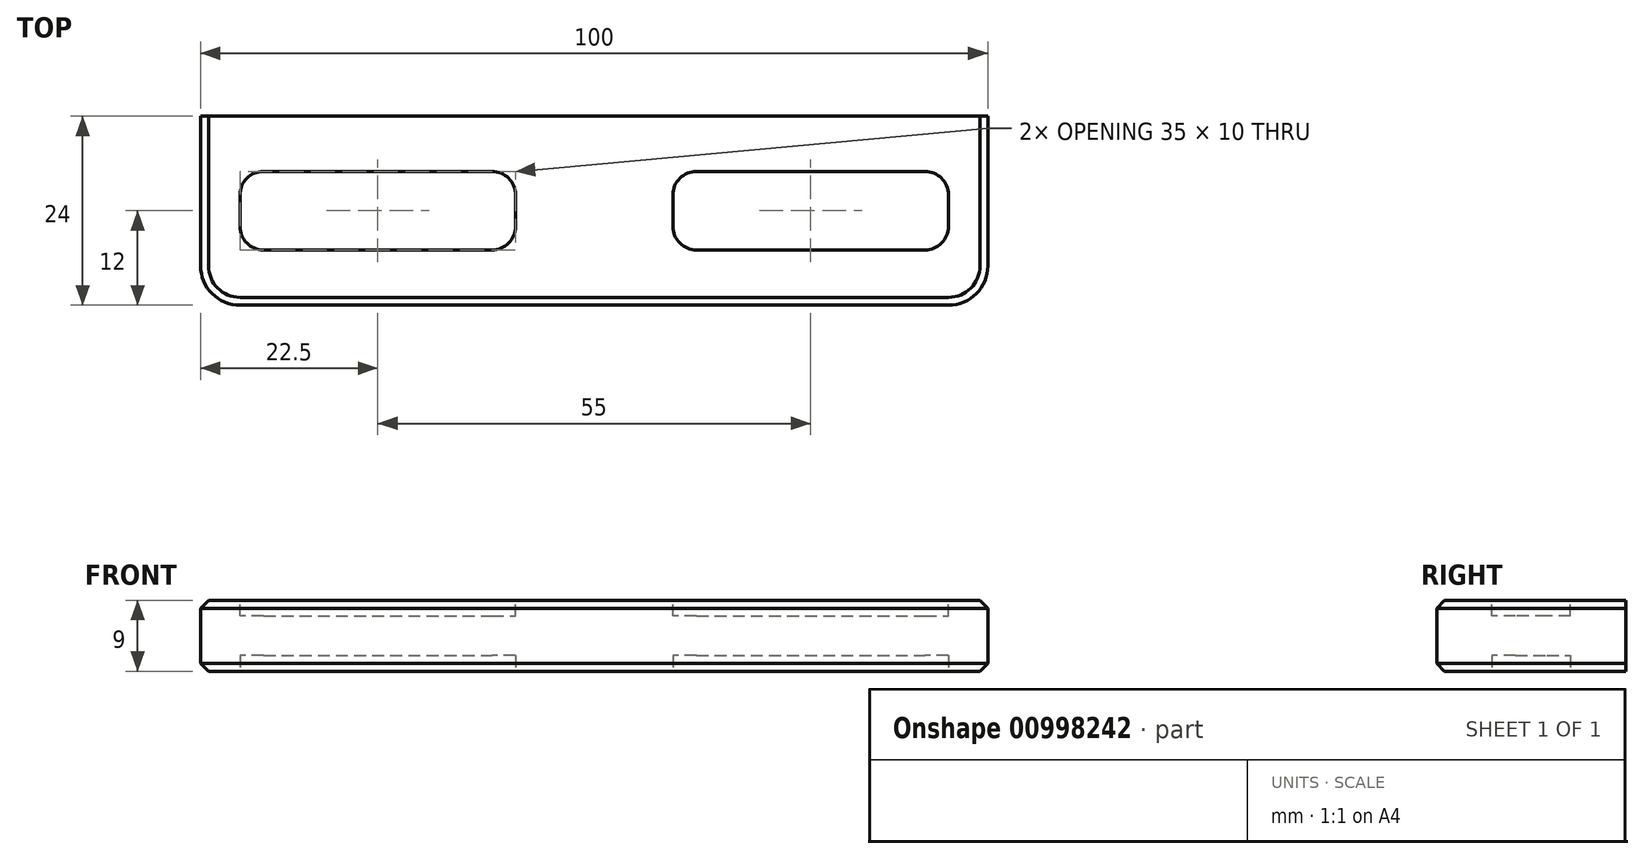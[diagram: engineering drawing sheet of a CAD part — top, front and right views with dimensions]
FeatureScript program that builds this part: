
annotation { "Feature Type Name" : "Feature", "Feature Type Description" : "" }
export const myFeature = defineFeature(function(context is Context, id is Id, definition is map)
    precondition{}
    {
        {
            var Q0;
            Q0=qCreatedBy(makeId("Top.planeOp"),FACE);
            var sketch = newSketch(context, id + "F0", { "sketchPlane" : qUnion([Q0])});
            skLineSegment(sketch, "E0.bottom", {"start": v(-50, 24) * mm, "end": v(50, 24) * mm});
            skLineSegment(sketch, "E0.top", {"start": v(-50, 0) * mm, "end": v(50, 0) * mm});
            skLineSegment(sketch, "E0.left", {"start": v(-50, 24) * mm, "end": v(-50, 0) * mm});
            skLineSegment(sketch, "E0.right", {"start": v(50, 24) * mm, "end": v(50, 0) * mm});
            skSolve(sketch);
        }
        {
            var Q0;
            Q0=makeQuery(id+"F0.imprint","IMPRINT",FACE,{"disambiguationData":[TD([[makeQuery(id+"F0.imprint","IMPRINT",EDGE,{"derivedFrom":sQuery(id+"F0.wireOp",EDGE,"E0.bottom")}),-1.0]])]});
            extrude(context, id + "F1", {"entities" : qUnion([Q0]), "depth" : 9 * mm, "offsetDistance" : 25 * mm});
        }
        {
            var Q0;
            Q0=makeQuery(id+"F1.opExtrude","SWEPT_EDGE",EDGE,{"disambiguationData":[OSD([sQuery(id+"F0.wireOp",EDGE,"E0.top"),sQuery(id+"F0.wireOp",EDGE,"E0.left")])]});
            var Q1;
            Q1=makeQuery(id+"F1.opExtrude","SWEPT_EDGE",EDGE,{"disambiguationData":[OSD([sQuery(id+"F0.wireOp",EDGE,"E0.top"),sQuery(id+"F0.wireOp",EDGE,"E0.right")])]});
            fillet(context, id + "F2", {"entities" : qUnion([Q0, Q1]), "radius" : 5 * mm, "tangentPropagation" : true, "allowEdgeOverflow" : false});
        }
        {
            var Q0;
            Q0=makeQuery(id+"F1.opExtrude","CAP_FACE",FACE,{"disambiguationData":[OSD([sQuery(id+"F0.wireOp",EDGE,"E0.bottom"),sQuery(id+"F0.wireOp",EDGE,"E0.top"),sQuery(id+"F0.wireOp",EDGE,"E0.left"),sQuery(id+"F0.wireOp",EDGE,"E0.right")])],"isStart":false});
            var sketch = newSketch(context, id + "F3", { "sketchPlane" : qUnion([Q0])});
            skLineSegment(sketch, "E1.bottom", {"start": v(-45, 17) * mm, "end": v(-10, 17) * mm});
            skLineSegment(sketch, "E1.top", {"start": v(-45, 7) * mm, "end": v(-10, 7) * mm});
            skLineSegment(sketch, "E1.left", {"start": v(-45, 17) * mm, "end": v(-45, 7) * mm});
            skLineSegment(sketch, "E1.right", {"start": v(-10, 17) * mm, "end": v(-10, 7) * mm});
            skSolve(sketch);
        }
        {
            var Q0;
            Q0=makeQuery(id+"F3.imprint","IMPRINT",FACE,{"disambiguationData":[TD([[makeQuery(id+"F3.imprint","IMPRINT",EDGE,{"derivedFrom":sQuery(id+"F3.wireOp",EDGE,"E1.bottom")}),1.0]])]});
            var sketch = newSketch(context, id + "F4", { "sketchPlane" : qUnion([Q0])});
            skLineSegment(sketch, "E2.bottom", {"start": v(10, 17) * mm, "end": v(45, 17) * mm});
            skLineSegment(sketch, "E2.top", {"start": v(10, 7) * mm, "end": v(45, 7) * mm});
            skLineSegment(sketch, "E2.left", {"start": v(10, 17) * mm, "end": v(10, 7) * mm});
            skLineSegment(sketch, "E2.right", {"start": v(45, 17) * mm, "end": v(45, 7) * mm});
            skSolve(sketch);
        }
        {
            var Q0;
            Q0=makeQuery(id+"F3.imprint","IMPRINT",FACE,{"disambiguationData":[TD([[makeQuery(id+"F3.imprint","IMPRINT",EDGE,{"derivedFrom":sQuery(id+"F3.wireOp",EDGE,"E1.bottom")}),-1.0]])]});
            var Q1;
            Q1=makeQuery(id+"F4.imprint","IMPRINT",FACE,{"disambiguationData":[TD([[makeQuery(id+"F4.imprint","IMPRINT",EDGE,{"derivedFrom":sQuery(id+"F4.wireOp",EDGE,"E2.bottom")}),-1.0]])]});
            extrude(context, id + "F5", {"entities" : qUnion([Q0, Q1]), "operationType" : NewBodyOperationType.REMOVE, "oppositeDirection" : true, "depth" : 2 * mm, "offsetDistance" : 25 * mm});
        }
        {
            var Q0;
            Q0=makeQuery(id+"F5.boolean.opBoolean","COPY",EDGE,{"derivedFrom":makeQuery(id+"F5.opExtrude","SWEPT_EDGE",EDGE,{"disambiguationData":[OSD([sQuery(id+"F3.wireOp",EDGE,"E1.top"),sQuery(id+"F3.wireOp",EDGE,"E1.left")])]})});
            var Q1;
            Q1=makeQuery(id+"F5.boolean.opBoolean","COPY",EDGE,{"derivedFrom":makeQuery(id+"F5.opExtrude","SWEPT_EDGE",EDGE,{"disambiguationData":[OSD([sQuery(id+"F3.wireOp",EDGE,"E1.bottom"),sQuery(id+"F3.wireOp",EDGE,"E1.left")])]})});
            var Q2;
            Q2=makeQuery(id+"F5.boolean.opBoolean","COPY",EDGE,{"derivedFrom":makeQuery(id+"F5.opExtrude","SWEPT_EDGE",EDGE,{"disambiguationData":[OSD([sQuery(id+"F3.wireOp",EDGE,"E1.bottom"),sQuery(id+"F3.wireOp",EDGE,"E1.right")])]})});
            var Q3;
            Q3=makeQuery(id+"F5.boolean.opBoolean","COPY",EDGE,{"derivedFrom":makeQuery(id+"F5.opExtrude","SWEPT_EDGE",EDGE,{"disambiguationData":[OSD([sQuery(id+"F4.wireOp",EDGE,"E2.top"),sQuery(id+"F4.wireOp",EDGE,"E2.left")])]})});
            var Q4;
            Q4=makeQuery(id+"F5.boolean.opBoolean","COPY",EDGE,{"derivedFrom":makeQuery(id+"F5.opExtrude","SWEPT_EDGE",EDGE,{"disambiguationData":[OSD([sQuery(id+"F3.wireOp",EDGE,"E1.top"),sQuery(id+"F3.wireOp",EDGE,"E1.right")])]})});
            var Q5;
            Q5=makeQuery(id+"F5.boolean.opBoolean","COPY",EDGE,{"derivedFrom":makeQuery(id+"F5.opExtrude","SWEPT_EDGE",EDGE,{"disambiguationData":[OSD([sQuery(id+"F4.wireOp",EDGE,"E2.top"),sQuery(id+"F4.wireOp",EDGE,"E2.right")])]})});
            var Q6;
            Q6=makeQuery(id+"F5.boolean.opBoolean","COPY",EDGE,{"derivedFrom":makeQuery(id+"F5.opExtrude","SWEPT_EDGE",EDGE,{"disambiguationData":[OSD([sQuery(id+"F4.wireOp",EDGE,"E2.bottom"),sQuery(id+"F4.wireOp",EDGE,"E2.right")])]})});
            var Q7;
            Q7=makeQuery(id+"F5.boolean.opBoolean","COPY",EDGE,{"derivedFrom":makeQuery(id+"F5.opExtrude","SWEPT_EDGE",EDGE,{"disambiguationData":[OSD([sQuery(id+"F4.wireOp",EDGE,"E2.bottom"),sQuery(id+"F4.wireOp",EDGE,"E2.left")])]})});
            fillet(context, id + "F6", {"entities" : qUnion([Q0, Q1, Q2, Q3, Q4, Q5, Q6, Q7]), "radius" : 3 * mm, "tangentPropagation" : true, "allowEdgeOverflow" : false});
        }
        {
            var Q0;
            Q0=makeQuery(id+"F1.opExtrude","CAP_FACE",FACE,{"disambiguationData":[OSD([sQuery(id+"F0.wireOp",EDGE,"E0.bottom"),sQuery(id+"F0.wireOp",EDGE,"E0.top"),sQuery(id+"F0.wireOp",EDGE,"E0.left"),sQuery(id+"F0.wireOp",EDGE,"E0.right")])],"isStart":true});
            var sketch = newSketch(context, id + "F7", { "sketchPlane" : qUnion([Q0])});
            skLineSegment(sketch, "E3.bottom", {"start": v(-45, -7) * mm, "end": v(-10, -7) * mm});
            skLineSegment(sketch, "E3.top", {"start": v(-45, -17) * mm, "end": v(-10, -17) * mm});
            skLineSegment(sketch, "E3.left", {"start": v(-45, -7) * mm, "end": v(-45, -17) * mm});
            skLineSegment(sketch, "E3.right", {"start": v(-10, -7) * mm, "end": v(-10, -17) * mm});
            skLineSegment(sketch, "E4.bottom", {"start": v(10, -7) * mm, "end": v(45, -7) * mm});
            skLineSegment(sketch, "E4.top", {"start": v(10, -17) * mm, "end": v(45, -17) * mm});
            skLineSegment(sketch, "E4.left", {"start": v(10, -7) * mm, "end": v(10, -17) * mm});
            skLineSegment(sketch, "E4.right", {"start": v(45, -7) * mm, "end": v(45, -17) * mm});
            skSolve(sketch);
        }
        {
            var Q0;
            Q0 = qSketchRegion(id + "F7", true);
            extrude(context, id + "F8", {"entities" : qUnion([Q0]), "operationType" : NewBodyOperationType.REMOVE, "oppositeDirection" : true, "depth" : 2 * mm, "offsetDistance" : 25 * mm});
        }
        {
            var Q0;
            Q0=makeQuery(id+"F8.boolean.opBoolean","COPY",EDGE,{"derivedFrom":makeQuery(id+"F8.opExtrude","SWEPT_EDGE",EDGE,{"disambiguationData":[OSD([sQuery(id+"F7.wireOp",EDGE,"E4.top"),sQuery(id+"F7.wireOp",EDGE,"E4.right")])]})});
            var Q1;
            Q1=makeQuery(id+"F8.boolean.opBoolean","COPY",EDGE,{"derivedFrom":makeQuery(id+"F8.opExtrude","SWEPT_EDGE",EDGE,{"disambiguationData":[OSD([sQuery(id+"F7.wireOp",EDGE,"E3.top"),sQuery(id+"F7.wireOp",EDGE,"E3.right")])]})});
            var Q2;
            Q2=makeQuery(id+"F8.boolean.opBoolean","COPY",EDGE,{"derivedFrom":makeQuery(id+"F8.opExtrude","SWEPT_EDGE",EDGE,{"disambiguationData":[OSD([sQuery(id+"F7.wireOp",EDGE,"E4.top"),sQuery(id+"F7.wireOp",EDGE,"E4.left")])]})});
            var Q3;
            Q3=makeQuery(id+"F8.boolean.opBoolean","COPY",EDGE,{"derivedFrom":makeQuery(id+"F8.opExtrude","SWEPT_EDGE",EDGE,{"disambiguationData":[OSD([sQuery(id+"F7.wireOp",EDGE,"E3.top"),sQuery(id+"F7.wireOp",EDGE,"E3.left")])]})});
            var Q4;
            Q4=makeQuery(id+"F8.boolean.opBoolean","COPY",EDGE,{"derivedFrom":makeQuery(id+"F8.opExtrude","SWEPT_EDGE",EDGE,{"disambiguationData":[OSD([sQuery(id+"F7.wireOp",EDGE,"E4.bottom"),sQuery(id+"F7.wireOp",EDGE,"E4.left")])]})});
            var Q5;
            Q5=makeQuery(id+"F8.boolean.opBoolean","COPY",EDGE,{"derivedFrom":makeQuery(id+"F8.opExtrude","SWEPT_EDGE",EDGE,{"disambiguationData":[OSD([sQuery(id+"F7.wireOp",EDGE,"E3.bottom"),sQuery(id+"F7.wireOp",EDGE,"E3.left")])]})});
            var Q6;
            Q6=makeQuery(id+"F8.boolean.opBoolean","COPY",EDGE,{"derivedFrom":makeQuery(id+"F8.opExtrude","SWEPT_EDGE",EDGE,{"disambiguationData":[OSD([sQuery(id+"F7.wireOp",EDGE,"E3.bottom"),sQuery(id+"F7.wireOp",EDGE,"E3.right")])]})});
            var Q7;
            Q7=makeQuery(id+"F8.boolean.opBoolean","COPY",EDGE,{"derivedFrom":makeQuery(id+"F8.opExtrude","SWEPT_EDGE",EDGE,{"disambiguationData":[OSD([sQuery(id+"F7.wireOp",EDGE,"E4.bottom"),sQuery(id+"F7.wireOp",EDGE,"E4.right")])]})});
            fillet(context, id + "F9", {"entities" : qUnion([Q0, Q1, Q2, Q3, Q4, Q5, Q6, Q7]), "radius" : 3 * mm, "tangentPropagation" : true, "allowEdgeOverflow" : false});
        }
        {
            var Q0;
            Q0=makeQuery(id+"F1.opExtrude","CAP_EDGE",EDGE,{"disambiguationData":[OSD([sQuery(id+"F0.wireOp",EDGE,"E0.top")])],"isStart":false});
            var Q1;
            Q1=makeQuery(id+"F1.opExtrude","CAP_EDGE",EDGE,{"disambiguationData":[OSD([sQuery(id+"F0.wireOp",EDGE,"E0.top")])],"isStart":true});
            chamfer(context, id + "F10", {"entities" : qUnion([Q0, Q1]), "width" : 1 * mm, "tangentPropagation" : true});
        }
    });
